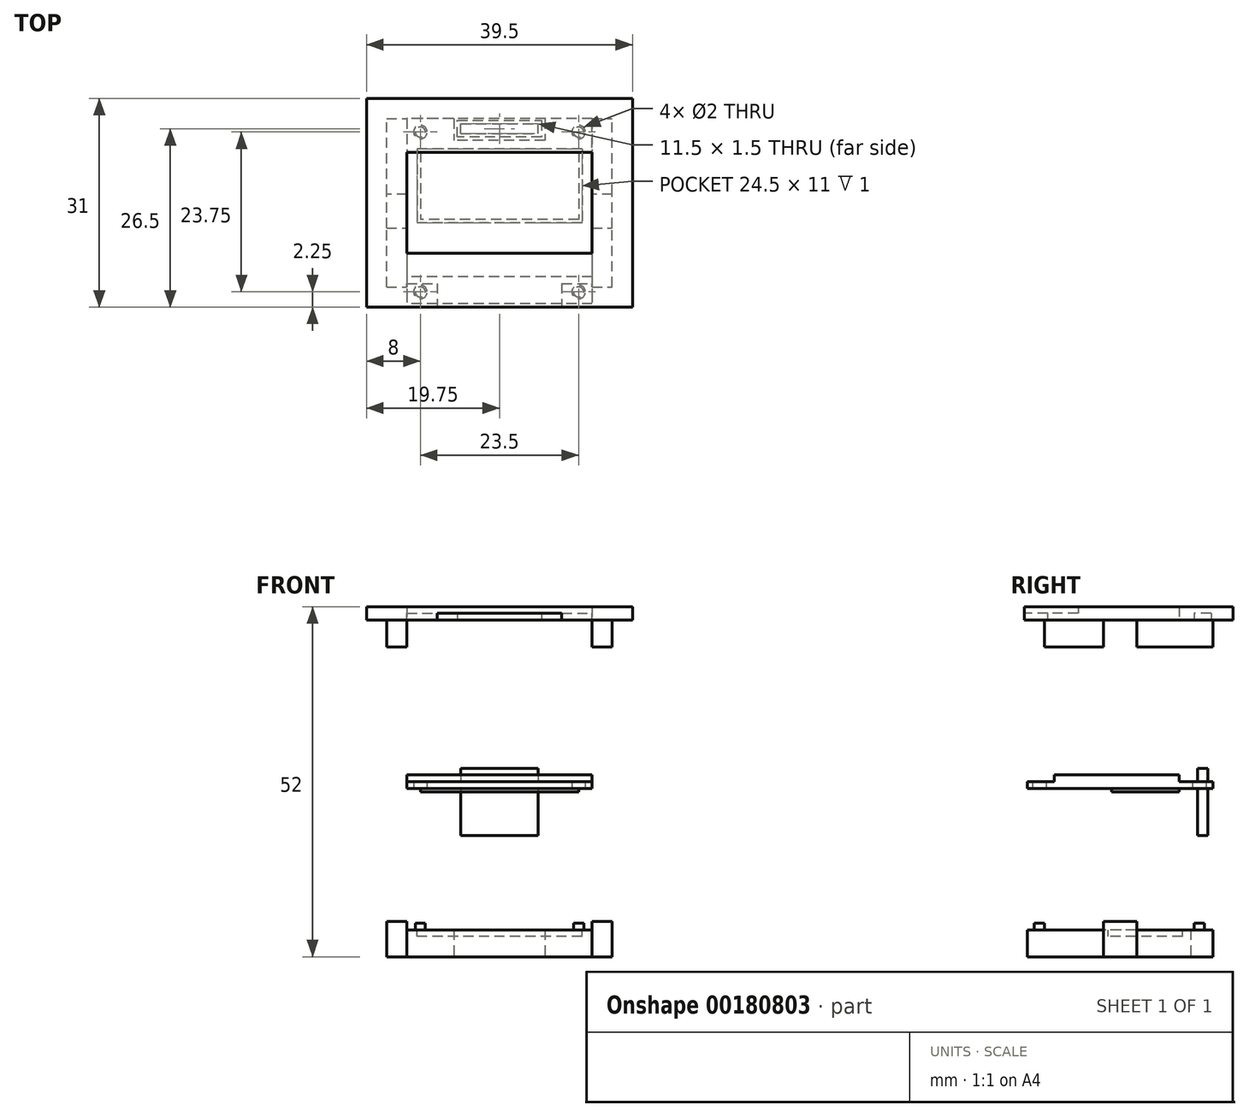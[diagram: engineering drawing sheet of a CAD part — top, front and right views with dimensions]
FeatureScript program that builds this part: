
annotation { "Feature Type Name" : "Feature", "Feature Type Description" : "" }
export const myFeature = defineFeature(function(context is Context, id is Id, definition is map)
    precondition{}
    {
        {
            var Q0;
            Q0=qCreatedBy(makeId("Top.planeOp"),FACE);
            var sketch = newSketch(context, id + "F0", { "sketchPlane" : qUnion([Q0])});
            skLineSegment(sketch, "E0.bottom", {"start": v(13.75, 13.75) * mm, "end": v(-13.75, 13.75) * mm});
            skLineSegment(sketch, "E0.top", {"start": v(13.75, -13.75) * mm, "end": v(-13.75, -13.75) * mm});
            skLineSegment(sketch, "E0.left", {"start": v(13.75, 13.75) * mm, "end": v(13.75, -13.75) * mm});
            skLineSegment(sketch, "E0.right", {"start": v(-13.75, 13.75) * mm, "end": v(-13.75, -13.75) * mm});
            skPoint(sketch, "E0.middle", {"position": v(0, 0) * mm});
            skCircle(sketch, "E1", {"center": v(-11.75, 11.75) * mm, "radius": 1 * mm});
            skCircle(sketch, "E2.1.0", {"center": v(-11.75, -12) * mm, "radius": 1 * mm});
            skCircle(sketch, "E2.2.0", {"center": v(11.75, -12) * mm, "radius": 1 * mm});
            skCircle(sketch, "E2.3.0", {"center": v(11.75, 11.75) * mm, "radius": 1 * mm});
            skLineSegment(sketch, "E3", {"start": v(-11.75, 11.75) * mm, "end": v(-11.75, -12) * mm, "construction": true});
            skLineSegment(sketch, "E4", {"start": v(11.75, -12) * mm, "end": v(-11.75, -12) * mm, "construction": true});
            skLineSegment(sketch, "E5", {"start": v(11.75, -12) * mm, "end": v(11.75, 11.75) * mm, "construction": true});
            skLineSegment(sketch, "E6", {"start": v(11.75, 11.75) * mm, "end": v(-11.75, 11.75) * mm, "construction": true});
            skSolve(sketch);
        }
        {
            var Q0;
            Q0=makeQuery(id+"F0.imprint","IMPRINT",FACE,{"disambiguationData":[TD([[makeQuery(id+"F0.imprint","IMPRINT",EDGE,{"derivedFrom":sQuery(id+"F0.wireOp",EDGE,"E0.bottom")}),1.0]])]});
            extrude(context, id + "F1", {"entities" : qUnion([Q0]), "depth" : 1 * mm, "offsetDistance" : 25 * mm});
        }
        {
            var Q0;
            Q0=qCreatedBy(makeId("Right.planeOp"),FACE);
            var sketch = newSketch(context, id + "F2", { "sketchPlane" : qUnion([Q0])});
            skLineSegment(sketch, "E7.0", {"start": v(13.75, 1) * mm, "end": v(-13.75, 1) * mm});
            skLineSegment(sketch, "E8", {"start": v(8.75, 1) * mm, "end": v(8.75, 2) * mm});
            skLineSegment(sketch, "E9", {"start": v(8.75, 2) * mm, "end": v(-9.75, 2) * mm});
            skLineSegment(sketch, "E10", {"start": v(-9.75, 2) * mm, "end": v(-9.75, 1) * mm});
            skSolve(sketch);
        }
        {
            var Q0;
            {var subQ0=sQuery(id+"F2.wireOp",EDGE,"E8");Q0=makeQuery(id+"F2.imprint","IMPRINT",FACE,{"disambiguationData":[TD([[makeQuery(id+"F2.imprint","IMPRINT",EDGE,{"derivedFrom":subQ0}),1.0]])]});}
            var Q1;
            Q1=makeQuery(id+"F1.opExtrude","SWEPT_FACE",FACE,{"disambiguationData":[OSD([sQuery(id+"F0.wireOp",EDGE,"E0.left")])]});
            var Q2;
            Q2=makeQuery(id+"F1.opExtrude","SWEPT_FACE",FACE,{"disambiguationData":[OSD([sQuery(id+"F0.wireOp",EDGE,"E0.right")])]});
            extrude(context, id + "F3", {"entities" : qUnion([Q0]), "operationType" : NewBodyOperationType.ADD, "endBound" : BoundingType.UP_TO_SURFACE, "depth" : 25 * mm, "endBoundEntityFace" : qUnion([Q1]), "offsetDistance" : 25 * mm, "hasSecondDirection" : true, "secondDirectionBound" : SecondDirectionBoundingType.UP_TO_SURFACE, "secondDirectionOppositeDirection" : true, "secondDirectionDepth" : 25 * mm, "secondDirectionBoundEntityFace" : qUnion([Q2])});
        }
        {
            var Q0;
            {var subQ0=sQuery(id+"F0.wireOp",EDGE,"E1");var subQ1=sQuery(id+"F0.wireOp",EDGE,"E0.left");var subQ2=sQuery(id+"F0.wireOp",EDGE,"E0.right");var subQ3=sQuery(id+"F0.wireOp",EDGE,"E0.bottom");var subQ4=sQuery(id+"F0.wireOp",EDGE,"E2.3.0");Q0=makeQuery(id+"F3.boolean.opBoolean","SPLIT",FACE,{"disambiguationData":[TD([makeQuery(id+"F1.opExtrude","SWEPT_FACE",FACE,{"disambiguationData":[OSD([subQ3])]})])],"derivedFrom":makeQuery(id+"F1.opExtrude","CAP_FACE",FACE,{"disambiguationData":[OSD([subQ3,sQuery(id+"F0.wireOp",EDGE,"E0.top"),subQ1,subQ2,subQ0,sQuery(id+"F0.wireOp",EDGE,"E2.1.0"),sQuery(id+"F0.wireOp",EDGE,"E2.2.0"),subQ4])],"isStart":false})});}
            var sketch = newSketch(context, id + "F4", { "sketchPlane" : qUnion([Q0])});
            skLineSegment(sketch, "E11.bottom", {"start": v(5.75, 13) * mm, "end": v(-5.75, 13) * mm});
            skLineSegment(sketch, "E11.top", {"start": v(5.75, 11.5) * mm, "end": v(-5.75, 11.5) * mm});
            skLineSegment(sketch, "E11.left", {"start": v(5.75, 13) * mm, "end": v(5.75, 11.5) * mm});
            skLineSegment(sketch, "E11.right", {"start": v(-5.75, 13) * mm, "end": v(-5.75, 11.5) * mm});
            skPoint(sketch, "E11.middle", {"position": v(0, 12.25) * mm});
            skSolve(sketch);
        }
        {
            var Q0;
            Q0=makeQuery(id+"F4.imprint","IMPRINT",FACE,{"disambiguationData":[TD([[makeQuery(id+"F4.imprint","IMPRINT",EDGE,{"derivedFrom":sQuery(id+"F4.wireOp",EDGE,"E11.bottom")}),1.0]])]});
            extrude(context, id + "F5", {"entities" : qUnion([Q0]), "operationType" : NewBodyOperationType.ADD, "depth" : 2 * mm, "offsetDistance" : 25 * mm, "hasSecondDirection" : true, "secondDirectionOppositeDirection" : true, "secondDirectionDepth" : 8 * mm});
        }
        {
            var Q0;
            Q0=makeQuery(id+"F1.opExtrude","CAP_FACE",FACE,{"disambiguationData":[OSD([sQuery(id+"F0.wireOp",EDGE,"E0.bottom"),sQuery(id+"F0.wireOp",EDGE,"E0.top"),sQuery(id+"F0.wireOp",EDGE,"E0.left"),sQuery(id+"F0.wireOp",EDGE,"E0.right"),sQuery(id+"F0.wireOp",EDGE,"E1"),sQuery(id+"F0.wireOp",EDGE,"E2.1.0"),sQuery(id+"F0.wireOp",EDGE,"E2.2.0"),sQuery(id+"F0.wireOp",EDGE,"E2.3.0")])],"isStart":true});
            var sketch = newSketch(context, id + "F6", { "sketchPlane" : qUnion([Q0])});
            skLineSegment(sketch, "E12.bottom", {"start": v(11.75, -8.75) * mm, "end": v(-11.75, -8.75) * mm});
            skLineSegment(sketch, "E12.top", {"start": v(11.75, 1.25) * mm, "end": v(-11.75, 1.25) * mm});
            skLineSegment(sketch, "E12.left", {"start": v(11.75, -8.75) * mm, "end": v(11.75, 1.25) * mm});
            skLineSegment(sketch, "E12.right", {"start": v(-11.75, -8.75) * mm, "end": v(-11.75, 1.25) * mm});
            skSolve(sketch);
        }
        {
            var Q0;
            Q0=makeQuery(id+"F6.imprint","IMPRINT",FACE,{"disambiguationData":[TD([[makeQuery(id+"F6.imprint","IMPRINT",EDGE,{"derivedFrom":sQuery(id+"F6.wireOp",EDGE,"E12.bottom")}),-1.0]])]});
            extrude(context, id + "F7", {"entities" : qUnion([Q0]), "operationType" : NewBodyOperationType.ADD, "depth" : 0.5 * mm, "offsetDistance" : 25 * mm});
        }
        {
            var Q0;
            Q0=qCreatedBy(makeId("Top.planeOp"),FACE);
            cPlane(context, id + "F8", {"entities" : qUnion([Q0]), "cplaneType" : CPlaneType.OFFSET, "offset" : 25 * mm, "width" : 150 * mm, "height" : 150 * mm});
        }
        {
            var Q0;
            Q0=qCreatedBy(id+"F8.planeOp",FACE);
            var sketch = newSketch(context, id + "F9", { "sketchPlane" : qUnion([Q0])});
            skLineSegment(sketch, "E13.0", {"start": v(13.75, 8.75) * mm, "end": v(13.75, -9.75) * mm});
            skLineSegment(sketch, "E13.1", {"start": v(-13.75, 8.75) * mm, "end": v(-13.75, -9.75) * mm});
            skLineSegment(sketch, "E13.2", {"start": v(13.75, 8.75) * mm, "end": v(-13.75, 8.75) * mm});
            skLineSegment(sketch, "E13.3", {"start": v(13.75, -9.75) * mm, "end": v(-13.75, -9.75) * mm});
            skLineSegment(sketch, "E14", {"start": v(-13.75, -6.25) * mm, "end": v(13.75, -6.25) * mm});
            skLineSegment(sketch, "E15.bottom", {"start": v(-19.75, 16.75) * mm, "end": v(19.75, 16.75) * mm});
            skLineSegment(sketch, "E15.top", {"start": v(-19.75, -14.25) * mm, "end": v(19.75, -14.25) * mm});
            skLineSegment(sketch, "E15.left", {"start": v(-19.75, 16.75) * mm, "end": v(-19.75, -14.25) * mm});
            skLineSegment(sketch, "E15.right", {"start": v(19.75, 16.75) * mm, "end": v(19.75, -14.25) * mm});
            skSolve(sketch);
        }
        {
            var Q0;
            {var subQ4=sQuery(id+"F9.wireOp",EDGE,"E13.2");Q0=makeQuery(id+"F9.imprint","IMPRINT",FACE,{"disambiguationData":[TD([[makeQuery(id+"F9.imprint","IMPRINT",EDGE,{"derivedFrom":subQ4}),-1.0]])]});}
            var Q1;
            {var subQ0=sQuery(id+"F9.wireOp",EDGE,"E13.3");Q1=makeQuery(id+"F9.imprint","IMPRINT",FACE,{"disambiguationData":[TD([[makeQuery(id+"F9.imprint","IMPRINT",EDGE,{"derivedFrom":subQ0}),-1.0]])]});}
            extrude(context, id + "F10", {"entities" : qUnion([Q0, Q1]), "depth" : 2 * mm, "offsetDistance" : 25 * mm});
        }
        {
            var Q0;
            Q0=makeQuery(id+"F10.opExtrude","CAP_FACE",FACE,{"disambiguationData":[OSD([sQuery(id+"F9.wireOp",EDGE,"E13.0"),sQuery(id+"F9.wireOp",EDGE,"E13.1"),sQuery(id+"F9.wireOp",EDGE,"E13.2"),sQuery(id+"F9.wireOp",EDGE,"E14"),sQuery(id+"F9.wireOp",EDGE,"E15.bottom"),sQuery(id+"F9.wireOp",EDGE,"E15.top"),sQuery(id+"F9.wireOp",EDGE,"E15.left"),sQuery(id+"F9.wireOp",EDGE,"E15.right")])],"isStart":true});
            var sketch = newSketch(context, id + "F11", { "sketchPlane" : qUnion([Q0])});
            skLineSegment(sketch, "E16.0", {"start": v(19.75, 9.75) * mm, "end": v(-19.75, 9.75) * mm});
            skLineSegment(sketch, "E17.0", {"start": v(19.75, -16.75) * mm, "end": v(19.75, 14.25) * mm});
            skLineSegment(sketch, "E17.1", {"start": v(-19.75, 14.25) * mm, "end": v(19.75, 14.25) * mm});
            skLineSegment(sketch, "E17.2", {"start": v(-19.75, -16.75) * mm, "end": v(-19.75, 14.25) * mm});
            skLineSegment(sketch, "E18.0", {"start": v(-19.75, 6.25) * mm, "end": v(19.75, 6.25) * mm});
            skPoint(sketch, "E19.orphan", {"position": v(-13.75, 6.25) * mm});
            skPoint(sketch, "E20.orphan", {"position": v(13.75, 6.25) * mm});
            skLineSegment(sketch, "E21.0", {"start": v(-13.75, -8.75) * mm, "end": v(-13.75, 14.25) * mm});
            skLineSegment(sketch, "E21.1", {"start": v(13.75, -8.75) * mm, "end": v(13.75, 14.25) * mm});
            skLineSegment(sketch, "E22.0.0", {"start": v(5.75, -11.5) * mm, "end": v(-5.75, -11.5) * mm});
            skLineSegment(sketch, "E22.0.1", {"start": v(-5.75, -11.5) * mm, "end": v(-5.75, -13) * mm});
            skLineSegment(sketch, "E22.0.2", {"start": v(-5.75, -13) * mm, "end": v(5.75, -13) * mm});
            skLineSegment(sketch, "E22.0.3", {"start": v(5.75, -13) * mm, "end": v(5.75, -11.5) * mm});
            skLineSegment(sketch, "E23.0", {"start": v(6.25, -11) * mm, "end": v(-6.25, -11) * mm});
            skLineSegment(sketch, "E23.1", {"start": v(6.25, -13.5) * mm, "end": v(6.25, -11) * mm});
            skLineSegment(sketch, "E23.2", {"start": v(-6.25, -13.5) * mm, "end": v(6.25, -13.5) * mm});
            skLineSegment(sketch, "E23.3", {"start": v(-6.25, -11) * mm, "end": v(-6.25, -13.5) * mm});
            skSolve(sketch);
        }
        {
            var Q0;
            {var subQ0=sQuery(id+"F11.wireOp",EDGE,"E21.1");var subQ1=sQuery(id+"F11.wireOp",EDGE,"E16.0");var subQ2=makeQuery(id+"F11.imprint","INTERSECT",VERTEX,{"derivedFrom":[subQ1,subQ0]});Q0=makeQuery(id+"F11.imprint","IMPRINT",FACE,{"disambiguationData":[TD([[makeQuery(id+"F11.imprint","IMPRINT",EDGE,{"disambiguationData":[TD([[subQ2,-1.0]])],"derivedFrom":subQ1}),1.0]])]});}
            var Q1;
            {var subQ0=sQuery(id+"F11.wireOp",EDGE,"E21.1");var subQ1=sQuery(id+"F11.wireOp",EDGE,"E16.0");var subQ2=makeQuery(id+"F11.imprint","INTERSECT",VERTEX,{"derivedFrom":[subQ1,subQ0]});Q1=makeQuery(id+"F11.imprint","IMPRINT",FACE,{"disambiguationData":[TD([[makeQuery(id+"F11.imprint","IMPRINT",EDGE,{"disambiguationData":[TD([[subQ2,-1.0]])],"derivedFrom":subQ1}),-1.0]])]});}
            var Q2;
            Q2=makeQuery(id+"F11.imprint","IMPRINT",FACE,{"disambiguationData":[TD([[makeQuery(id+"F11.imprint","IMPRINT",EDGE,{"derivedFrom":sQuery(id+"F11.wireOp",EDGE,"E22.0.0")}),-1.0]])]});
            var Q3;
            Q3=makeQuery(id+"F11.imprint","IMPRINT",FACE,{"disambiguationData":[TD([[makeQuery(id+"F11.imprint","IMPRINT",EDGE,{"derivedFrom":sQuery(id+"F11.wireOp",EDGE,"E22.0.0")}),1.0]])]});
            extrude(context, id + "F12", {"entities" : qUnion([Q0, Q1, Q2, Q3]), "operationType" : NewBodyOperationType.REMOVE, "oppositeDirection" : true, "depth" : 1 * mm, "offsetDistance" : 25 * mm});
        }
        {
            var Q0;
            Q0=makeQuery(id+"F10.opExtrude","CAP_FACE",FACE,{"disambiguationData":[OSD([sQuery(id+"F9.wireOp",EDGE,"E13.0"),sQuery(id+"F9.wireOp",EDGE,"E13.1"),sQuery(id+"F9.wireOp",EDGE,"E13.2"),sQuery(id+"F9.wireOp",EDGE,"E14"),sQuery(id+"F9.wireOp",EDGE,"E15.bottom"),sQuery(id+"F9.wireOp",EDGE,"E15.top"),sQuery(id+"F9.wireOp",EDGE,"E15.left"),sQuery(id+"F9.wireOp",EDGE,"E15.right")])],"isStart":true});
            var sketch = newSketch(context, id + "F13", { "sketchPlane" : qUnion([Q0])});
            skLineSegment(sketch, "E24.bottom", {"start": v(-13.75, 14.25) * mm, "end": v(-16.75, 14.25) * mm});
            skLineSegment(sketch, "E24.top", {"start": v(-13.75, -16.75) * mm, "end": v(-16.75, -16.75) * mm});
            skLineSegment(sketch, "E24.left", {"start": v(-13.75, 14.25) * mm, "end": v(-13.75, -16.75) * mm});
            skLineSegment(sketch, "E24.right", {"start": v(-16.75, 14.25) * mm, "end": v(-16.75, -16.75) * mm});
            skLineSegment(sketch, "E25.bottom", {"start": v(13.75, 14.25) * mm, "end": v(16.75, 14.25) * mm});
            skLineSegment(sketch, "E25.top", {"start": v(13.75, -16.75) * mm, "end": v(16.75, -16.75) * mm});
            skLineSegment(sketch, "E25.left", {"start": v(13.75, 14.25) * mm, "end": v(13.75, -16.75) * mm});
            skLineSegment(sketch, "E25.right", {"start": v(16.75, 14.25) * mm, "end": v(16.75, -16.75) * mm});
            skLineSegment(sketch, "E26", {"start": v(-16.75, 11.25) * mm, "end": v(-13.75, 11.25) * mm});
            skLineSegment(sketch, "E27", {"start": v(-16.75, -13.75) * mm, "end": v(-13.75, -13.75) * mm});
            skLineSegment(sketch, "E28", {"start": v(-13.75, -13.75) * mm, "end": v(13.75, -13.75) * mm, "construction": true});
            skLineSegment(sketch, "E29", {"start": v(13.75, -13.75) * mm, "end": v(16.75, -13.75) * mm});
            skLineSegment(sketch, "E30", {"start": v(-13.75, 11.25) * mm, "end": v(13.75, 11.25) * mm, "construction": true});
            skLineSegment(sketch, "E31", {"start": v(13.75, 11.25) * mm, "end": v(16.75, 11.25) * mm});
            skLineSegment(sketch, "E32", {"start": v(-16.75, 0) * mm, "end": v(16.75, 0) * mm, "construction": true});
            skLineSegment(sketch, "E33", {"start": v(-16.75, 2.5) * mm, "end": v(16.75, 2.5) * mm});
            skLineSegment(sketch, "E34", {"start": v(16.75, -2.5) * mm, "end": v(-16.75, -2.5) * mm});
            skSolve(sketch);
        }
        {
            var Q0;
            {var subQ0=sQuery(id+"F13.wireOp",EDGE,"E26");Q0=makeQuery(id+"F13.imprint","IMPRINT",FACE,{"disambiguationData":[TD([[makeQuery(id+"F13.imprint","IMPRINT",EDGE,{"derivedFrom":subQ0}),-1.0]])]});}
            var Q1;
            {var subQ0=sQuery(id+"F13.wireOp",EDGE,"E29");Q1=makeQuery(id+"F13.imprint","IMPRINT",FACE,{"disambiguationData":[TD([[makeQuery(id+"F13.imprint","IMPRINT",EDGE,{"derivedFrom":subQ0}),1.0]])]});}
            var Q2;
            {var subQ0=sQuery(id+"F13.wireOp",EDGE,"E27");Q2=makeQuery(id+"F13.imprint","IMPRINT",FACE,{"disambiguationData":[TD([[makeQuery(id+"F13.imprint","IMPRINT",EDGE,{"derivedFrom":subQ0}),1.0]])]});}
            var Q3;
            {var subQ0=sQuery(id+"F13.wireOp",EDGE,"E31");Q3=makeQuery(id+"F13.imprint","IMPRINT",FACE,{"disambiguationData":[TD([[makeQuery(id+"F13.imprint","IMPRINT",EDGE,{"derivedFrom":subQ0}),-1.0]])]});}
            extrude(context, id + "F14", {"entities" : qUnion([Q0, Q1, Q2, Q3]), "operationType" : NewBodyOperationType.ADD, "depth" : 4 * mm, "offsetDistance" : 25 * mm});
        }
        {
            var Q0;
            Q0=makeQuery(id+"F12.boolean.opBoolean","COPY",FACE,{"derivedFrom":makeQuery(id+"F12.opExtrude","CAP_FACE",FACE,{"disambiguationData":[OSD([sQuery(id+"F11.wireOp",EDGE,"E17.1"),sQuery(id+"F11.wireOp",EDGE,"E18.0"),sQuery(id+"F11.wireOp",EDGE,"E21.0"),sQuery(id+"F11.wireOp",EDGE,"E21.1")])],"isStart":false})});
            var sketch = newSketch(context, id + "F15", { "sketchPlane" : qUnion([Q0])});
            skLineSegment(sketch, "E35", {"start": v(-13.75, 10.75) * mm, "end": v(-9.25, 10.75) * mm});
            skLineSegment(sketch, "E36", {"start": v(-9.25, 10.75) * mm, "end": v(-9.25, 14.25) * mm});
            skLineSegment(sketch, "E37", {"start": v(-9.25, 10.75) * mm, "end": v(9.25, 10.75) * mm});
            skLineSegment(sketch, "E38", {"start": v(9.25, 10.75) * mm, "end": v(9.25, 10.75) * mm});
            skLineSegment(sketch, "E39", {"start": v(9.25, 10.75) * mm, "end": v(9.25, 14.25) * mm});
            skLineSegment(sketch, "E40", {"start": v(9.25, 10.75) * mm, "end": v(13.75, 10.75) * mm});
            skSolve(sketch);
        }
        {
            var Q0;
            {var subQ0=sQuery(id+"F15.wireOp",EDGE,"E35");Q0=makeQuery(id+"F15.imprint","IMPRINT",FACE,{"disambiguationData":[TD([[makeQuery(id+"F15.imprint","IMPRINT",EDGE,{"derivedFrom":subQ0}),1.0]])]});}
            var Q1;
            {var subQ0=sQuery(id+"F15.wireOp",EDGE,"E39");Q1=makeQuery(id+"F15.imprint","IMPRINT",FACE,{"disambiguationData":[TD([[makeQuery(id+"F15.imprint","IMPRINT",EDGE,{"derivedFrom":subQ0}),-1.0]])]});}
            var Q2;
            Q2=makeQuery(id+"F10.opExtrude","CAP_FACE",FACE,{"disambiguationData":[OSD([sQuery(id+"F9.wireOp",EDGE,"E13.0"),sQuery(id+"F9.wireOp",EDGE,"E13.1"),sQuery(id+"F9.wireOp",EDGE,"E13.2"),sQuery(id+"F9.wireOp",EDGE,"E14"),sQuery(id+"F9.wireOp",EDGE,"E15.bottom"),sQuery(id+"F9.wireOp",EDGE,"E15.top"),sQuery(id+"F9.wireOp",EDGE,"E15.left"),sQuery(id+"F9.wireOp",EDGE,"E15.right")])],"isStart":true});
            extrude(context, id + "F16", {"entities" : qUnion([Q0, Q1]), "operationType" : NewBodyOperationType.ADD, "endBound" : BoundingType.UP_TO_SURFACE, "depth" : 25 * mm, "endBoundEntityFace" : qUnion([Q2]), "offsetDistance" : 25 * mm});
        }
        {
            var Q0;
            Q0=qCreatedBy(makeId("Top.planeOp"),FACE);
            cPlane(context, id + "F17", {"entities" : qUnion([Q0]), "cplaneType" : CPlaneType.OFFSET, "offset" : 25 * mm, "oppositeDirection" : true, "width" : 150 * mm, "height" : 150 * mm});
        }
        {
            var Q0;
            Q0=qCreatedBy(id+"F17.planeOp",FACE);
            var sketch = newSketch(context, id + "F18", { "sketchPlane" : qUnion([Q0])});
            skLineSegment(sketch, "E41.0", {"start": v(-19.75, -14.25) * mm, "end": v(-9.25, -14.25) * mm, "construction": true});
            skLineSegment(sketch, "E41.1", {"start": v(-16.75, -14.25) * mm, "end": v(-16.75, -2.5) * mm, "construction": true});
            skLineSegment(sketch, "E41.2", {"start": v(16.75, 2.5) * mm, "end": v(16.75, 16.75) * mm, "construction": true});
            skLineSegment(sketch, "E41.3", {"start": v(-19.75, 16.75) * mm, "end": v(19.75, 16.75) * mm, "construction": true});
            skPoint(sketch, "E42.orphan", {"position": v(-16.75, -11.25) * mm});
            skPoint(sketch, "E43.orphan", {"position": v(16.75, 13.75) * mm});
            skLineSegment(sketch, "E44.bottom", {"start": v(-16.75, -14.25) * mm, "end": v(16.75, -14.25) * mm, "construction": true});
            skLineSegment(sketch, "E44.top", {"start": v(-16.75, 16.75) * mm, "end": v(16.75, 16.75) * mm});
            skLineSegment(sketch, "E44.left", {"start": v(-16.75, -14.25) * mm, "end": v(-16.75, 16.75) * mm});
            skLineSegment(sketch, "E44.right", {"start": v(16.75, -14.25) * mm, "end": v(16.75, 16.75) * mm});
            skLineSegment(sketch, "E45", {"start": v(16.75, 13.75) * mm, "end": v(-16.75, 13.75) * mm});
            skLineSegment(sketch, "E46.0", {"start": v(16.75, -13.75) * mm, "end": v(-16.75, -13.75) * mm});
            skPoint(sketch, "E47.orphan", {"position": v(-13.75, -13.75) * mm});
            skPoint(sketch, "E48.orphan", {"position": v(13.75, -13.75) * mm});
            skSolve(sketch);
        }
        {
            var Q0;
            Q0=makeQuery(id+"F18.imprint","IMPRINT",FACE,{"disambiguationData":[TD([[makeQuery(id+"F18.imprint","IMPRINT",EDGE,{"derivedFrom":sQuery(id+"F18.wireOp",EDGE,"E44.bottom")}),1.0]])]});
            var Q1;
            {var subQ0=sQuery(id+"F18.wireOp",EDGE,"E45");Q1=makeQuery(id+"F18.imprint","IMPRINT",FACE,{"disambiguationData":[TD([[makeQuery(id+"F18.imprint","IMPRINT",EDGE,{"derivedFrom":subQ0}),1.0]])]});}
            extrude(context, id + "F19", {"entities" : qUnion([Q0, Q1]), "depth" : 4 * mm, "offsetDistance" : 25 * mm});
        }
        {
            var Q0;
            Q0=makeQuery(id+"F19.opExtrude","CAP_FACE",FACE,{"disambiguationData":[OSD([sQuery(id+"F18.wireOp",EDGE,"E44.bottom"),sQuery(id+"F18.wireOp",EDGE,"E44.top"),sQuery(id+"F18.wireOp",EDGE,"E44.left"),sQuery(id+"F18.wireOp",EDGE,"E44.right")])],"isStart":false});
            var sketch = newSketch(context, id + "F20", { "sketchPlane" : qUnion([Q0])});
            skLineSegment(sketch, "E49", {"start": v(0, 13.75) * mm, "end": v(0, -13.75) * mm, "construction": true});
            skLineSegment(sketch, "E50", {"start": v(-16.75, 0) * mm, "end": v(16.75, 0) * mm, "construction": true});
            skPoint(sketch, "E51", {"position": v(0, 0) * mm});
            skLineSegment(sketch, "E52.0", {"start": v(16.75, 13.75) * mm, "end": v(-16.75, 13.75) * mm});
            skLineSegment(sketch, "E53.0", {"start": v(16.75, -13.75) * mm, "end": v(-16.75, -13.75) * mm});
            skCircle(sketch, "E54.0", {"center": v(-11.75, 11.75) * mm, "radius": 1 * mm, "construction": true});
            skCircle(sketch, "E54.1", {"center": v(-11.75, -12) * mm, "radius": 1 * mm, "construction": true});
            skCircle(sketch, "E54.2", {"center": v(11.75, -12) * mm, "radius": 1 * mm, "construction": true});
            skCircle(sketch, "E54.3", {"center": v(11.75, 11.75) * mm, "radius": 1 * mm, "construction": true});
            skCircle(sketch, "E55.0", {"center": v(-11.75, -12) * mm, "radius": 0.75 * mm});
            skCircle(sketch, "E56.0", {"center": v(11.75, -12) * mm, "radius": 0.75 * mm});
            skCircle(sketch, "E57.0", {"center": v(11.75, 11.75) * mm, "radius": 0.75 * mm});
            skCircle(sketch, "E58.0", {"center": v(-11.75, 11.75) * mm, "radius": 0.75 * mm});
            skSolve(sketch);
        }
        {
            var Q0;
            Q0 = qSketchRegion(id + "F20", true);
            extrude(context, id + "F21", {"entities" : qUnion([Q0]), "operationType" : NewBodyOperationType.ADD, "depth" : 1 * mm, "offsetDistance" : 25 * mm});
        }
        {
            var Q0;
            Q0=makeQuery(id+"F19.opExtrude","CAP_FACE",FACE,{"disambiguationData":[OSD([sQuery(id+"F18.wireOp",EDGE,"E44.bottom"),sQuery(id+"F18.wireOp",EDGE,"E44.top"),sQuery(id+"F18.wireOp",EDGE,"E44.left"),sQuery(id+"F18.wireOp",EDGE,"E44.right")])],"isStart":false});
            var sketch = newSketch(context, id + "F22", { "sketchPlane" : qUnion([Q0])});
            skLineSegment(sketch, "E59.0", {"start": v(-16.75, -2.5) * mm, "end": v(-13.75, -2.5) * mm});
            skLineSegment(sketch, "E59.1", {"start": v(-13.75, 2.5) * mm, "end": v(-16.75, 2.5) * mm});
            skLineSegment(sketch, "E59.2", {"start": v(13.75, -2.5) * mm, "end": v(16.75, -2.5) * mm});
            skLineSegment(sketch, "E59.3", {"start": v(16.75, 2.5) * mm, "end": v(13.75, 2.5) * mm});
            skLineSegment(sketch, "E60", {"start": v(-16.75, 2.5) * mm, "end": v(-16.75, -2.5) * mm});
            skLineSegment(sketch, "E61", {"start": v(-13.75, -2.5) * mm, "end": v(-13.75, 2.5) * mm});
            skLineSegment(sketch, "E62", {"start": v(13.75, 2.5) * mm, "end": v(13.75, -2.5) * mm});
            skLineSegment(sketch, "E63", {"start": v(16.75, -2.5) * mm, "end": v(16.75, 2.5) * mm});
            skSolve(sketch);
        }
        {
            var Q0;
            Q0 = qSketchRegion(id + "F22", true);
            extrude(context, id + "F23", {"entities" : qUnion([Q0]), "operationType" : NewBodyOperationType.ADD, "depth" : 1.25 * mm, "offsetDistance" : 25 * mm});
        }
        {
            var Q0;
            Q0=makeQuery(id+"F19.opExtrude","CAP_FACE",FACE,{"disambiguationData":[OSD([sQuery(id+"F18.wireOp",EDGE,"E44.bottom"),sQuery(id+"F18.wireOp",EDGE,"E44.top"),sQuery(id+"F18.wireOp",EDGE,"E44.left"),sQuery(id+"F18.wireOp",EDGE,"E44.right")])],"isStart":true});
            var sketch = newSketch(context, id + "F24", { "sketchPlane" : qUnion([Q0])});
            skLineSegment(sketch, "E64.0", {"start": v(-16.75, 2.5) * mm, "end": v(-13.75, 2.5) * mm});
            skLineSegment(sketch, "E64.1", {"start": v(-16.75, -13.75) * mm, "end": v(-16.75, -13.75) * mm});
            skLineSegment(sketch, "E64.2", {"start": v(-13.75, -2.5) * mm, "end": v(-16.75, -2.5) * mm});
            skLineSegment(sketch, "E64.3", {"start": v(13.75, 2.5) * mm, "end": v(16.75, 2.5) * mm});
            skLineSegment(sketch, "E64.4", {"start": v(16.75, -2.5) * mm, "end": v(13.75, -2.5) * mm});
            skLineSegment(sketch, "E64.5", {"start": v(16.75, -13.75) * mm, "end": v(16.75, -13.75) * mm});
            skLineSegment(sketch, "E64.6", {"start": v(-16.75, -13.75) * mm, "end": v(16.75, -13.75) * mm});
            skLineSegment(sketch, "E64.7", {"start": v(-16.75, -13.75) * mm, "end": v(16.75, -13.75) * mm});
            skLineSegment(sketch, "E64.8", {"start": v(-13.75, 2.5) * mm, "end": v(-13.75, -2.5) * mm});
            skLineSegment(sketch, "E64.9", {"start": v(13.75, -2.5) * mm, "end": v(13.75, 2.5) * mm});
            skLineSegment(sketch, "E65", {"start": v(-13.75, 2.5) * mm, "end": v(-13.75, 13.75) * mm});
            skLineSegment(sketch, "E66", {"start": v(-13.75, -13.75) * mm, "end": v(-13.75, -13.75) * mm});
            skLineSegment(sketch, "E67", {"start": v(13.75, 2.5) * mm, "end": v(13.75, 13.75) * mm});
            skLineSegment(sketch, "E68", {"start": v(13.75, -2.5) * mm, "end": v(13.75, -13.75) * mm});
            skLineSegment(sketch, "E69.0", {"start": v(5.75, -13) * mm, "end": v(-5.75, -13) * mm, "construction": true});
            skLineSegment(sketch, "E69.1", {"start": v(5.75, -11.5) * mm, "end": v(-5.75, -11.5) * mm, "construction": true});
            skLineSegment(sketch, "E69.2", {"start": v(5.75, -13) * mm, "end": v(5.75, -11.5) * mm, "construction": true});
            skLineSegment(sketch, "E69.3", {"start": v(-5.75, -13) * mm, "end": v(-5.75, -11.5) * mm, "construction": true});
            skLineSegment(sketch, "E69.4", {"start": v(13.75, -13.75) * mm, "end": v(-13.75, -13.75) * mm, "construction": true});
            skLineSegment(sketch, "E70.0", {"start": v(-6.75, -14) * mm, "end": v(-6.75, -10.5) * mm});
            skLineSegment(sketch, "E70.1", {"start": v(6.75, -14) * mm, "end": v(-6.75, -14) * mm, "construction": true});
            skLineSegment(sketch, "E70.2", {"start": v(6.75, -14) * mm, "end": v(6.75, -10.5) * mm});
            skLineSegment(sketch, "E70.3", {"start": v(6.75, -10.5) * mm, "end": v(-6.75, -10.5) * mm});
            skLineSegment(sketch, "E71.0", {"start": v(16.75, -13.75) * mm, "end": v(-16.75, -13.75) * mm});
            skLineSegment(sketch, "E72", {"start": v(6.75, -13.75) * mm, "end": v(6.75, -14) * mm});
            skLineSegment(sketch, "E73", {"start": v(-6.75, -13.75) * mm, "end": v(-6.75, -14) * mm});
            skLineSegment(sketch, "E74.0", {"start": v(16.75, 13.75) * mm, "end": v(-16.75, 13.75) * mm});
            skLineSegment(sketch, "E75.1", {"start": v(-13.75, -13.75) * mm, "end": v(-13.75, 13.75) * mm});
            skSolve(sketch);
        }
        {
            var Q0;
            {var subQ0=sQuery(id+"F24.wireOp",EDGE,"E64.0");Q0=makeQuery(id+"F24.imprint","IMPRINT",FACE,{"disambiguationData":[TD([[makeQuery(id+"F24.imprint","IMPRINT",EDGE,{"derivedFrom":subQ0}),1.0]])]});}
            var Q1;
            {var subQ0=sQuery(id+"F24.wireOp",EDGE,"E64.4");Q1=makeQuery(id+"F24.imprint","IMPRINT",FACE,{"disambiguationData":[TD([[makeQuery(id+"F24.imprint","IMPRINT",EDGE,{"derivedFrom":subQ0}),1.0]])]});}
            var Q2;
            {var subQ3=sQuery(id+"F24.wireOp",EDGE,"E64.2");Q2=makeQuery(id+"F24.imprint","IMPRINT",FACE,{"disambiguationData":[TD([[makeQuery(id+"F24.imprint","IMPRINT",EDGE,{"derivedFrom":subQ3}),1.0]])]});}
            var Q3;
            {var subQ0=sQuery(id+"F24.wireOp",EDGE,"E64.3");Q3=makeQuery(id+"F24.imprint","IMPRINT",FACE,{"disambiguationData":[TD([[makeQuery(id+"F24.imprint","IMPRINT",EDGE,{"derivedFrom":subQ0}),1.0]])]});}
            var Q4;
            Q4=makeQuery(id+"F24.imprint","IMPRINT",FACE,{"disambiguationData":[TD([[makeQuery(id+"F24.imprint","IMPRINT",EDGE,{"derivedFrom":sQuery(id+"F24.wireOp",EDGE,"E70.0")}),-1.0]])]});
            extrude(context, id + "F25", {"entities" : qUnion([Q0, Q1, Q2, Q3, Q4]), "operationType" : NewBodyOperationType.REMOVE, "endBound" : BoundingType.UP_TO_NEXT, "oppositeDirection" : true, "depth" : 25 * mm, "offsetDistance" : 25 * mm});
        }
        {
            var Q0;
            Q0=makeQuery(id+"F19.opExtrude","CAP_FACE",FACE,{"disambiguationData":[OSD([sQuery(id+"F18.wireOp",EDGE,"E44.left"),sQuery(id+"F18.wireOp",EDGE,"E44.right"),sQuery(id+"F18.wireOp",EDGE,"E45"),sQuery(id+"F18.wireOp",EDGE,"E46.0")])],"isStart":false});
            var sketch = newSketch(context, id + "F26", { "sketchPlane" : qUnion([Q0])});
            skLineSegment(sketch, "E76.0", {"start": v(-12.25, 9.25) * mm, "end": v(-12.25, -1.75) * mm});
            skLineSegment(sketch, "E76.1", {"start": v(12.25, 9.25) * mm, "end": v(-12.25, 9.25) * mm});
            skLineSegment(sketch, "E76.2", {"start": v(12.25, 9.25) * mm, "end": v(12.25, -1.75) * mm});
            skLineSegment(sketch, "E76.3", {"start": v(12.25, -1.75) * mm, "end": v(-12.25, -1.75) * mm});
            skSolve(sketch);
        }
        {
            var Q0;
            Q0=makeQuery(id+"F26.imprint","IMPRINT",FACE,{"disambiguationData":[TD([[makeQuery(id+"F26.imprint","IMPRINT",EDGE,{"derivedFrom":sQuery(id+"F26.wireOp",EDGE,"E76.0")}),1.0]])]});
            extrude(context, id + "F27", {"entities" : qUnion([Q0]), "operationType" : NewBodyOperationType.REMOVE, "oppositeDirection" : true, "depth" : 1 * mm, "offsetDistance" : 25 * mm});
        }
    });
